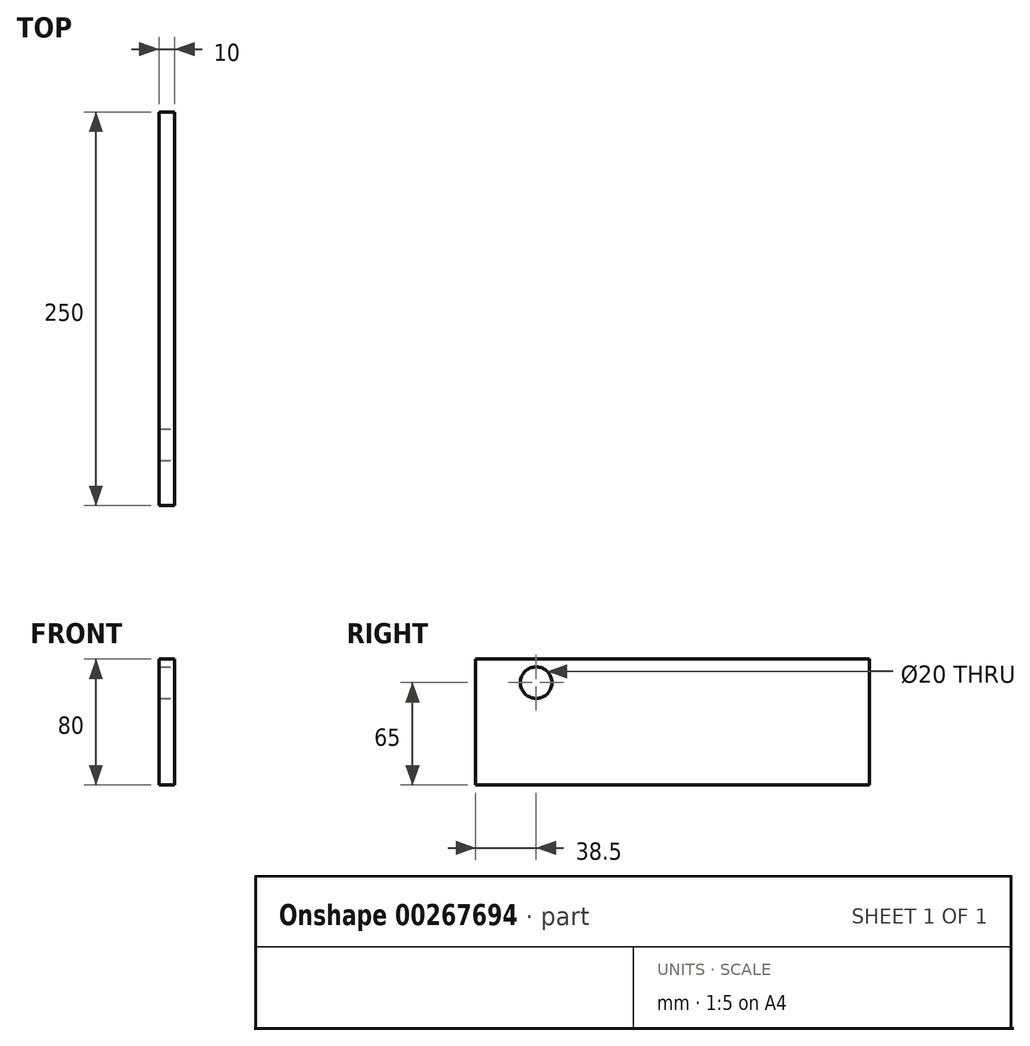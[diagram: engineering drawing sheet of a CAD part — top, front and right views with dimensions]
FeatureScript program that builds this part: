
annotation { "Feature Type Name" : "Feature", "Feature Type Description" : "" }
export const myFeature = defineFeature(function(context is Context, id is Id, definition is map)
    precondition{}
    {
        {
            var Q0;
            Q0=qCreatedBy(makeId("Front.planeOp"),FACE);
            var sketch = newSketch(context, id + "F0", { "sketchPlane" : qUnion([Q0])});
            skLineSegment(sketch, "E0.bottom", {"start": v(5, 40) * mm, "end": v(-5, 40) * mm});
            skLineSegment(sketch, "E0.top", {"start": v(5, -40) * mm, "end": v(-5, -40) * mm});
            skLineSegment(sketch, "E0.left", {"start": v(5, 40) * mm, "end": v(5, -40) * mm});
            skLineSegment(sketch, "E0.right", {"start": v(-5, 40) * mm, "end": v(-5, -40) * mm});
            skPoint(sketch, "E0.middle", {"position": v(0, 0) * mm});
            skSolve(sketch);
        }
        {
            var Q0;
            Q0=makeQuery(id+"F0.imprint","IMPRINT",FACE,{"disambiguationData":[TD([[makeQuery(id+"F0.imprint","IMPRINT",EDGE,{"derivedFrom":sQuery(id+"F0.wireOp",EDGE,"E0.bottom")}),1.0]])]});
            extrude(context, id + "F1", {"entities" : qUnion([Q0]), "oppositeDirection" : true, "depth" : (2 * 80 + 90) * mm});
        }
        {
            var Q0;
            Q0=makeQuery(id+"F1.opExtrude","SWEPT_FACE",FACE,{"disambiguationData":[OSD([sQuery(id+"F0.wireOp",EDGE,"E0.left")])]});
            var sketch = newSketch(context, id + "F2", { "sketchPlane" : qUnion([Q0])});
            skCircle(sketch, "E1", {"center": v(38.5, 25) * mm, "radius": 10 * mm});
            skSolve(sketch);
        }
        {
            var Q0;
            Q0=makeQuery(id+"F2.imprint","IMPRINT",FACE,{"disambiguationData":[TD([[makeQuery(id+"F2.imprint","IMPRINT",EDGE,{"derivedFrom":sQuery(id+"F2.wireOp",EDGE,"E1")}),1.0]])]});
            extrude(context, id + "F3", {"entities" : qUnion([Q0]), "operationType" : NewBodyOperationType.REMOVE, "endBound" : BoundingType.THROUGH_ALL, "oppositeDirection" : true, "depth" : 25 * mm});
        }
    });
